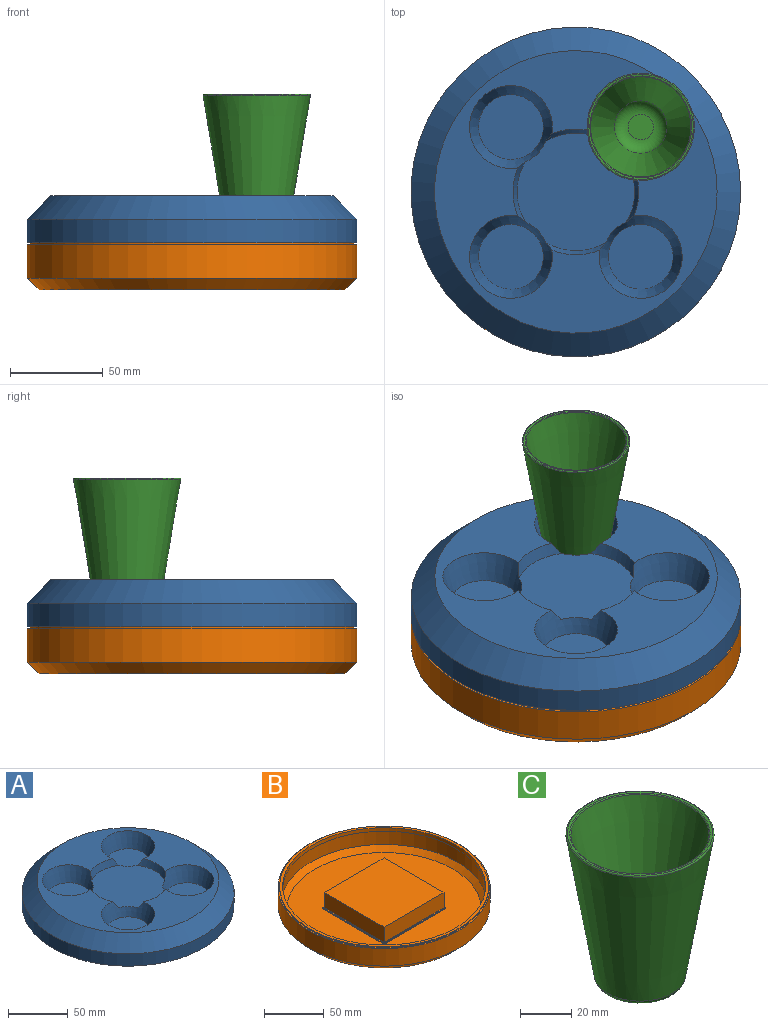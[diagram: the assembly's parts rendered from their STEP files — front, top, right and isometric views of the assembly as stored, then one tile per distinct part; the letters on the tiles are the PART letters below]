
ASSEMBLY  parts=3 mates=2
PART A: 33 faces, bbox 177.8x177.8x25.4 mm
  f0: cylinder r=88.9mm len=177.8mm, axis (0,0,-1), area 7093.9mm2, adj f2,f3
  f1: plane 152.4x152.4mm, normal (0,0,1), area 8814.5mm2, adj f3,f5,f7,f9,f11,f13,f14,f15
  f2: plane 177.8x177.8mm, normal (0,0,-1), area 1398.5mm2, adj f0,f17
  f3: cone r=76.2mm half-angle=45deg, axis (0,0,-1), area 9315.7mm2, adj f0,f1
  f4: plane 35x35mm, normal (0,0,1), area 962.1mm2, adj f5
  f5: cone r=17.5mm half-angle=18deg, axis (0,0,1), area 1826.7mm2, adj f1,f4,f12,f13,f16
  f6: plane 35x35mm, normal (0,0,1), area 962.1mm2, adj f7
  f7: cone r=17.5mm half-angle=18deg, axis (0,0,1), area 1826.7mm2, adj f1,f6,f12,f15,f16
  f8: plane 35x35mm, normal (0,0,1), area 962.1mm2, adj f9
  f9: cone r=17.5mm half-angle=18deg, axis (0,0,1), area 1826.7mm2, adj f1,f8,f12,f14,f15
  f10: plane 35x35mm, normal (0,0,1), area 962.1mm2, adj f11
  f11: cone r=17.5mm half-angle=18deg, axis (0,0,1), area 1826.7mm2, adj f1,f10,f12,f13,f14
  f12: plane 63.5x63.5mm, normal (0,0,1), area 3059mm2, adj f5,f7,f9,f11,f13,f14,f15,f16
  f13: cone r=31.75mm half-angle=19deg, axis (0,0,1), area 200.9mm2, adj f1,f5,f11,f12
  f14: cone r=31.75mm half-angle=19deg, axis (0,0,1), area 200.9mm2, adj f1,f9,f11,f12
  f15: cone r=31.75mm half-angle=19deg, axis (0,0,1), area 200.9mm2, adj f1,f7,f9,f12
  f16: cone r=31.75mm half-angle=19deg, axis (0,0,1), area 200.9mm2, adj f1,f5,f7,f12
  f17: cylinder r=86.36mm len=172.72mm, axis (0,0,-1), area 6320.3mm2, adj f2,f19
  f18: plane 150.3x150.3mm, normal (0,0,-1), area 7295.8mm2, adj f19,f21,f23,f25,f27,f29,f30,f31
  f19: cone r=74.4mm half-angle=45deg, axis (0,0,-1), area 8045.4mm2, adj f17,f18
  f20: plane 38.69x38.69mm, normal (0,0,-1), area 1175.7mm2, adj f21
  f21: cone r=19.92mm half-angle=18deg, axis (0,0,1), area 1948.8mm2, adj f18,f20,f28,f29,f32
  f22: plane 38.69x38.69mm, normal (0,0,-1), area 1175.7mm2, adj f23
  f23: cone r=19.92mm half-angle=18deg, axis (0,0,1), area 1948.8mm2, adj f18,f22,f28,f31,f32
  f24: plane 38.69x38.69mm, normal (0,0,-1), area 1175.7mm2, adj f25
  f25: cone r=19.92mm half-angle=18deg, axis (0,0,1), area 1948.8mm2, adj f18,f24,f28,f30,f31
  f26: plane 38.69x38.69mm, normal (0,0,-1), area 1175.7mm2, adj f27
  f27: cone r=19.92mm half-angle=18deg, axis (0,0,1), area 1948.8mm2, adj f18,f26,f28,f29,f30
  f28: plane 67.12x67.12mm, normal (0,0,-1), area 3119.8mm2, adj f21,f23,f25,f27,f29,f30,f31,f32
  f29: cone r=34.15mm half-angle=19deg, axis (0,0,1), area 164.2mm2, adj f18,f21,f27,f28
  f30: cone r=34.15mm half-angle=19deg, axis (0,0,1), area 164.2mm2, adj f18,f25,f27,f28
  f31: cone r=34.15mm half-angle=19deg, axis (0,0,1), area 164.2mm2, adj f18,f23,f25,f28
  f32: cone r=34.15mm half-angle=19deg, axis (0,0,1), area 164.2mm2, adj f18,f21,f23,f28
PART B: 31 faces, bbox 177.8x177.8x25.4 mm
  f0: cylinder r=88.9mm len=177.8mm, axis (0,0,-1), area 10082.3mm2, adj f2,f14
  f1: plane 165.1x165.1mm, normal (0,0,-1), area 16784.4mm2, adj f2,f3,f4,f5,f6
  f2: cone r=88.9mm half-angle=45deg, axis (0,0,1), area 4837mm2, adj f0,f1
  f3: plane 68x1mm, normal (0,1,0), area 68mm2, adj f1,f4,f6,f7
  f4: plane 68x1mm, normal (-1,0,0), area 68mm2, adj f1,f3,f5,f7
  f5: plane 68x1mm, normal (0,-1,0), area 68mm2, adj f1,f4,f6,f7
  f6: plane 68x1mm, normal (1,0,0), area 68mm2, adj f1,f3,f5,f7
  f7: plane 68x68mm, normal (0,0,-1), area 268mm2, adj f3,f4,f5,f6,f8,f9,f10,f11
  f8: plane 66x15.51mm, normal (0,-1,0), area 1023.7mm2, adj f7,f9,f11,f12
  f9: plane 66x15.51mm, normal (1,0,0), area 1023.7mm2, adj f7,f8,f10,f12
  f10: plane 66x15.51mm, normal (0,1,0), area 1023.7mm2, adj f7,f9,f11,f12
  f11: plane 66x15.51mm, normal (-1,0,0), area 1023.7mm2, adj f7,f8,f10,f12
  f12: plane 66x66mm, normal (0,0,-1), area 4356mm2, adj f8,f9,f10,f11
  f13: cylinder r=87.63mm len=175.26mm, axis (0,0,1), area 550.6mm2, adj f14,f15
  f14: plane 177.8x177.8mm, normal (0,0,1), area 704.3mm2, adj f0,f13
  f15: plane 175.26x175.26mm, normal (0,0,1), area 1378.2mm2, adj f13,f29
  f16: cylinder r=86.36mm len=172.72mm, axis (0,0,-1), area 7845.1mm2, adj f18,f30
  f17: plane 163x163mm, normal (0,0,1), area 15525.5mm2, adj f18,f19,f20,f21,f22
  f18: cone r=87.1mm half-angle=45deg, axis (0,0,1), area 3626mm2, adj f16,f17
  f19: plane 73.08x1mm, normal (0,-1,0), area 73.1mm2, adj f17,f20,f22,f23
  f20: plane 73.08x1mm, normal (1,0,0), area 73.1mm2, adj f17,f19,f21,f23
  f21: plane 73.08x1mm, normal (0,1,0), area 73.1mm2, adj f17,f20,f22,f23
  f22: plane 73.08x1mm, normal (-1,0,0), area 73.1mm2, adj f17,f19,f21,f23
  f23: plane 73.08x73.08mm, normal (0,0,1), area 288.3mm2, adj f19,f20,f21,f22,f24,f25,f26,f27
  f24: plane 71.08x15.51mm, normal (0,1,0), area 1102.5mm2, adj f23,f25,f27,f28
  f25: plane 71.08x15.51mm, normal (-1,0,0), area 1102.5mm2, adj f23,f24,f26,f28
  f26: plane 71.08x15.51mm, normal (0,-1,0), area 1102.5mm2, adj f23,f25,f27,f28
  f27: plane 71.08x15.51mm, normal (1,0,0), area 1102.5mm2, adj f23,f24,f26,f28
  f28: plane 71.08x71.08mm, normal (0,0,1), area 5052.4mm2, adj f24,f25,f26,f27
  f29: cylinder r=85.09mm len=170.18mm, axis (0,0,1), area 1892.6mm2, adj f15,f30
  f30: plane 172.72x172.72mm, normal (0,0,-1), area 684.1mm2, adj f16,f29
PART C: 9 faces, bbox 62.7x62.7x69.9 mm
  f0: cone r=28.98mm half-angle=9.4deg, axis (0,0,1), area 10021.3mm2, adj f1,f8
  f1: torus R=15.35mm, axis (0,0,-1), area 378.4mm2, adj f0,f2
  f2: plane 30.69x30.69mm, normal (0,0,-1), area 739.8mm2, adj f1
  f3: plane 13.66x13.66mm, normal (0,0,1), area 146.6mm2, adj f4
  f4: torus R=6.83mm, axis (0,0,-1), area 716.8mm2, adj f3,f5
  f5: cone r=14.24mm half-angle=13.4deg, axis (0,0,1), area 7173.7mm2, adj f4,f6
  f6: torus R=27.51mm, axis (0,0,-1), area 102.6mm2, adj f5,f7
  f7: cone r=27.44mm half-angle=82.2deg, axis (0,0,1), area 171.8mm2, adj f6,f8
  f8: torus R=28.48mm, axis (0,0,-1), area 169.3mm2, adj f0,f7
PLACE A t=(-17.19,-46.08,11.35)mm
PLACE B t=(166.96,-46.08,-14.05)mm
PLACE C t=(17.81,-11.08,21.75)mm
MATE fastened C.f0 <-> A.f11  axis (0,0,-1) through (17.81,-11.08,21.75)mm
MATE fastened A.f0 <-> B.f13  axis (0,0,-1) through (-17.19,-46.08,11.35)mm
